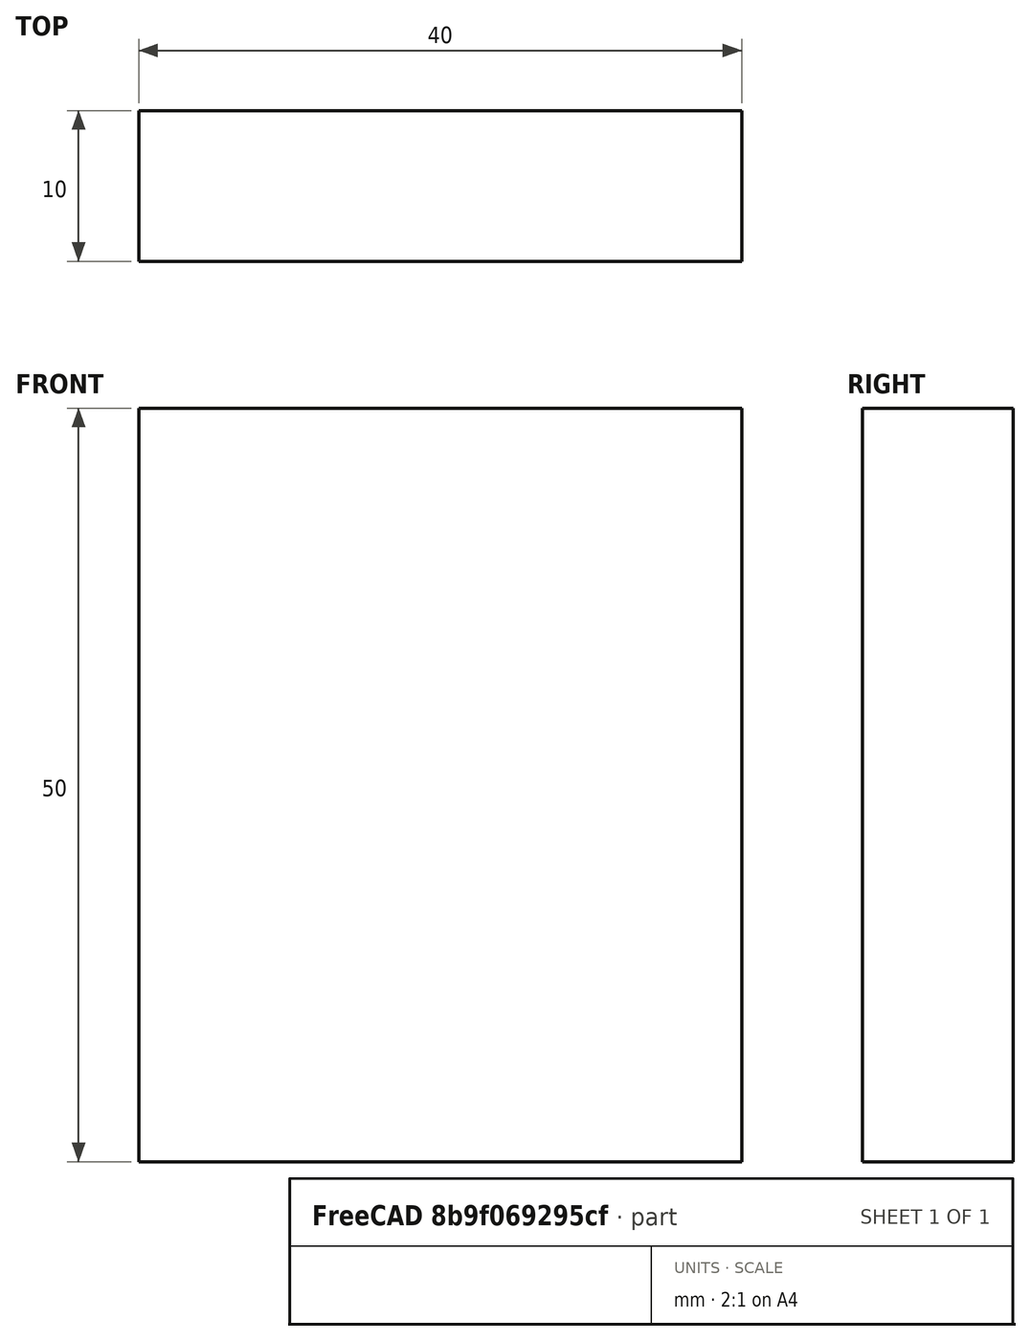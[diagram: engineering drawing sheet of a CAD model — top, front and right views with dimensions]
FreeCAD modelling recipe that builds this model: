
FCSTD DOCUMENT  (FreeCAD 0.15R4671 (Git))
Label: Flat Bar 40x10 EN10058 S235JR
License: All rights reserved
LicenseURL: http://en.wikipedia.org/wiki/All_rights_reserved
objects: Sketcher::SketchObject×1, Part::Extrusion×1
note: 2 computed .brp shape members not serialized (recipe doc carries the construction recipe); baked Part::Feature solids carry a one-line shape summary decoded from their .brp

FEATURE [Sketcher::SketchObject] Sketch
  sketch-geometry (4):
    g0: LineSegment StartX=-20 StartY=-5 StartZ=0 EndX=20 EndY=-5 EndZ=0
    g1: LineSegment StartX=20 StartY=-5 StartZ=0 EndX=20 EndY=5 EndZ=0
    g2: LineSegment StartX=20 StartY=5 StartZ=0 EndX=-20 EndY=5 EndZ=0
    g3: LineSegment StartX=-20 StartY=5 StartZ=0 EndX=-20 EndY=-5 EndZ=0
  constraints (12):
    c: Coincident(g0,g1)
    c: Coincident(g1,g2)
    c: Coincident(g2,g3)
    c: Coincident(g3,g0)
    c: Horizontal(g0)
    c: Horizontal(g2)
    c: Vertical(g1)
    c: Vertical(g3)
    c: Symmetric(g1,g2,g-2)
    c: Symmetric(g0,g1,g-1)
    c: DistanceY(g1) = 10
    c: DistanceX(g0) = 40
FEATURE [Part::Extrusion] Extrude  label="Flat Bar 40x10 EN10058 S235JR"
  Base = -> Sketch
  Dir = (0,0,50)
  Solid = true
